# Revit family: AFDV-C_Horizontal_Floor_Mount
name_source: partatom
category: Mechanical Equipment
units: mm (PartAtom-declared; Revit-internal decimal feet)

## family parameters
Always vertical = Yes
Cut with Voids When Loaded = No
Part Type = Normal
Room Calculation Point = No
Round Connector Dimension = Use Radius
Shared = No
Work Plane-Based = No

## types (11) — shared parameters
0 = 0' - 0"
1" = 0' - 1"
1.5 = 0' - 1 1/2"
2" = 0' - 2"
2' = 2' - 0"
3" = 0' - 3"
30 = 30.00°
4" = 0' - 4"
60 = 60.00°
Manufacturer = Loren Cook Company
Model = AFDV-C
ONE EIGTH = 0' - 0 1/8"
P = 0' - 0 9/16"
P/2 = 0' - 0 9/32"
Type Comments = Tube Axial Fan Horizontal Floor Mount Direct Drive Arrangement 4
URL = www.lorencook.com

## per-type parameters (varying)
- 12_AFDV-C_HOR_FLOOR: (A+.25")/2=0' - 6 9/16"; (E-.25")/2=0' - 10 7/8"; -(E-.25")/2=-0' - 10 7/8"; -E/2=-0' - 11"; A=1' - 0 7/8"; A/2=0' - 6 7/16"; A/3=0' - 5 5/32"; B=1' - 3 11/16"; B/2=0' - 7 27/32"; C=1' - 2 5/8"; C/2=0' - 7 5/16"; C/2+J=1' - 5 1/16"; E=1' - 10"; E-2"=1' - 8"; E/2=0' - 11"; F=0' - 0 5/16"; F/2=0' - 0 5/32"; G=6' - 0"; H=1' - 8 1/8"; H/2=0' - 10 1/16"; J=0' - 0 15/16"; J-(C/2)=0' - 2 7/16"; K=0' - 9 3/4"; L=1' - 4"; L/2=0' - 8"; M=0' - 6"; VANE=0' - 6"
- 16_AFDV-C_HOR_FLOOR: (A+.25")/2=0' - 8 9/16"; (E-.25")/2=1' - 0 3/8"; -(E-.25")/2=-1' - 0 3/8"; -E/2=-1' - 0 1/2"; A=1' - 4 7/8"; A/2=0' - 8 7/16"; A/3=0' - 6 3/4"; B=1' - 7 11/16"; B/2=0' - 9 27/32"; C=1' - 6 5/8"; C/2=0' - 9 5/16"; C/2+J=1' - 9 1/16"; E=2' - 1"; E-2"=1' - 11"; E/2=1' - 0 1/2"; F=0' - 0 5/16"; F/2=0' - 0 5/32"; G=6' - 0"; H=1' - 11 1/8"; H/2=0' - 11 9/16"; J=0' - 0 15/16"; J-(C/2)=0' - 2 7/16"; K=0' - 11 3/4"; L=1' - 8"; L/2=0' - 10"; M=0' - 8"; VANE=0' - 10"
- 18_AFDV-C_HOR_FLOOR: (A+.25")/2=0' - 9 9/16"; (E-.25")/2=1' - 0 3/8"; -(E-.25")/2=-1' - 0 3/8"; -E/2=-1' - 0 1/2"; A=1' - 6 7/8"; A/2=0' - 9 7/16"; A/3=0' - 7 9/16"; B=1' - 9 11/16"; B/2=0' - 10 27/32"; C=1' - 8 5/8"; C/2=0' - 10 5/16"; C/2+J=1' - 11 1/16"; E=2' - 1"; E-2"=1' - 11"; E/2=1' - 0 1/2"; F=0' - 0 5/16"; F/2=0' - 0 5/32"; G=6' - 0"; H=1' - 11 1/8"; H/2=0' - 11 9/16"; J=0' - 0 15/16"; J-(C/2)=0' - 2 7/16"; K=1' - 0 3/4"; L=1' - 10"; L/2=0' - 11"; M=0' - 9"; VANE=0' - 11"
- 24_AFDV-C_HOR_FLOOR: (A+.25")/2=1' - 0 9/16"; (E-.25")/2=1' - 3 3/8"; -(E-.25")/2=-1' - 3 3/8"; -E/2=-1' - 3 1/2"; A=2' - 0 7/8"; A/2=1' - 0 7/16"; A/3=0' - 9 15/16"; B=2' - 5 1/8"; B/2=1' - 2 9/16"; C=2' - 2 7/8"; C/2=1' - 1 7/16"; C/2+J=2' - 5 7/16"; E=2' - 7"; E-2"=2' - 5"; E/2=1' - 3 1/2"; F=0' - 0 7/16"; F/2=0' - 0 7/32"; G=6' - 0"; H=2' - 5 1/8"; H/2=1' - 2 9/16"; J=0' - 0 15/16"; J-(C/2)=0' - 2 9/16"; K=1' - 4"; L=2' - 4 1/2"; L/2=1' - 2 1/4"; M=1' - 0 1/4"; VANE=1' - 1"
- 28_AFDV-C_HOR_FLOOR: (A+.25")/2=1' - 2 9/16"; (E-.25")/2=1' - 3 3/8"; -(E-.25")/2=-1' - 3 3/8"; -E/2=-1' - 3 1/2"; A=2' - 4 7/8"; A/2=1' - 2 7/16"; A/3=0' - 11 9/16"; B=2' - 9 1/8"; B/2=1' - 4 9/16"; C=2' - 6 7/8"; C/2=1' - 3 7/16"; C/2+J=2' - 9 7/16"; E=2' - 7"; E-2"=2' - 5"; E/2=1' - 3 1/2"; F=0' - 0 7/16"; F/2=0' - 0 7/32"; G=6' - 0"; H=2' - 5 1/8"; H/2=1' - 2 9/16"; J=0' - 0 15/16"; J-(C/2)=0' - 2 9/16"; K=1' - 6"; L=2' - 8 1/2"; L/2=1' - 4 1/4"; M=1' - 2 1/4"; VANE=1' - 1"
- 32_AFDV-C_HOR_FLOOR: (A+.25")/2=1' - 4 5/8"; (E-.25")/2=1' - 4 7/8"; -(E-.25")/2=-1' - 4 7/8"; -E/2=-1' - 5"; A=2' - 9"; A/2=1' - 4 1/2"; A/3=1' - 1 3/16"; B=3' - 1 1/4"; B/2=1' - 6 5/8"; C=2' - 11"; C/2=1' - 5 1/2"; C/2+J=3' - 1 5/8"; E=2' - 10"; E-2"=2' - 8"; E/2=1' - 5"; F=0' - 0 7/16"; F/2=0' - 0 7/32"; G=6' - 0"; H=2' - 8 1/8"; H/2=1' - 4 1/16"; J=0' - 0 15/16"; J-(C/2)=0' - 2 5/8"; K=1' - 8 1/8"; L=3' - 0 5/8"; L/2=1' - 6 5/16"; M=1' - 4 5/16"; VANE=1' - 3"
- 36_AFDV-C_HOR_FLOOR: (A+.25")/2=1' - 6 5/8"; (E-.25")/2=1' - 4 7/8"; -(E-.25")/2=-1' - 4 7/8"; -E/2=-1' - 5"; A=3' - 1"; A/2=1' - 6 1/2"; A/3=1' - 2 13/16"; B=3' - 5 3/8"; B/2=1' - 8 11/16"; C=3' - 3"; C/2=1' - 7 1/2"; C/2+J=3' - 5 5/8"; E=2' - 10"; E-2"=2' - 8"; E/2=1' - 5"; F=0' - 0 7/16"; F/2=0' - 0 7/32"; G=6' - 0"; H=2' - 8 1/8"; H/2=1' - 4 1/16"; J=0' - 0 15/16"; J-(C/2)=0' - 2 5/8"; K=1' - 10 1/8"; L=3' - 4 5/8"; L/2=1' - 8 5/16"; M=1' - 6 5/16"; VANE=1' - 4"
- 44_AFDV-C_HOR_FLOOR: (A+.25")/2=1' - 10 5/8"; (E-.25")/2=1' - 8 7/8"; -(E-.25")/2=-1' - 8 7/8"; -E/2=-1' - 9"; A=3' - 9"; A/2=1' - 10 1/2"; A/3=1' - 6"; B=4' - 1 3/8"; B/2=2' - 0 11/16"; C=3' - 11 1/2"; C/2=1' - 11 3/4"; C/2+J=4' - 1 7/8"; E=3' - 6"; E-2"=3' - 4"; E/2=1' - 9"; F=0' - 0 7/16"; F/2=0' - 0 7/32"; G=12' - 0"; H=3' - 4"; H/2=1' - 8"; J=0' - 1"; J-(C/2)=0' - 2 3/8"; K=2' - 2 1/8"; L=4' - 0 3/4"; L/2=2' - 0 3/8"; M=1' - 10 3/8"; VANE=1' - 7"
- 48_AFDV-C_HOR_FLOOR: (A+.25")/2=2' - 0 11/16"; (E-.25")/2=1' - 8 7/8"; -(E-.25")/2=-1' - 8 7/8"; -E/2=-1' - 9"; A=4' - 1 1/8"; A/2=2' - 0 9/16"; A/3=1' - 7 21/32"; B=4' - 5 1/2"; B/2=2' - 2 3/4"; C=4' - 3 5/8"; C/2=2' - 1 13/16"; C/2+J=4' - 6 9/16"; E=3' - 6"; E-2"=3' - 4"; E/2=1' - 9"; F=0' - 0 7/16"; F/2=0' - 0 7/32"; G=12' - 0"; H=3' - 4"; H/2=1' - 8"; J=0' - 1"; J-(C/2)=0' - 2 15/16"; K=2' - 4 3/4"; L=4' - 5 7/8"; L/2=2' - 2 15/16"; M=2' - 0 15/16"; VANE=1' - 10"
- 54_AFDV-C_HOR_FLOOR: (A+.25")/2=2' - 3 13/16"; (E-.25")/2=1' - 8 7/8"; -(E-.25")/2=-1' - 8 7/8"; -E/2=-1' - 9"; A=4' - 7 3/8"; A/2=2' - 3 11/16"; A/3=1' - 10 5/32"; B=5' - 0 3/4"; B/2=2' - 6 3/8"; C=4' - 9 5/8"; C/2=2' - 4 13/16"; C/2+J=5' - 0 11/16"; E=3' - 6"; E-2"=3' - 4"; E/2=1' - 9"; F=0' - 0 7/16"; F/2=0' - 0 7/32"; G=12' - 0"; H=3' - 3 3/4"; H/2=1' - 7 7/8"; J=0' - 1 1/8"; J-(C/2)=0' - 3 1/16"; K=2' - 7 7/8"; L=5' - 0 7/8"; L/2=2' - 6 7/16"; M=2' - 4 1/16"; VANE=1' - 11"
- 60_AFDV-C_HOR_FLOOR: (A+.25")/2=2' - 6 13/16"; (E-.25")/2=1' - 8 7/8"; -(E-.25")/2=-1' - 8 7/8"; -E/2=-1' - 9"; A=5' - 1 3/8"; A/2=2' - 6 11/16"; A/3=2' - 0 9/16"; B=5' - 6 3/4"; B/2=2' - 9 3/8"; C=5' - 3 5/8"; C/2=2' - 7 13/16"; C/2+J=5' - 6 11/16"; E=3' - 6"; E-2"=3' - 4"; E/2=1' - 9"; F=0' - 0 7/16"; F/2=0' - 0 7/32"; G=12' - 0"; H=3' - 3 3/4"; H/2=1' - 7 7/8"; J=0' - 1 1/8"; J-(C/2)=0' - 3 1/16"; K=2' - 10 7/8"; L=5' - 6 1/8"; L/2=2' - 9 1/16"; M=2' - 7 1/16"; VANE=2' - 1"

## geometry (parser evidence)
native form markers: Sweep x2
no freeform markers — native parametric forms only
